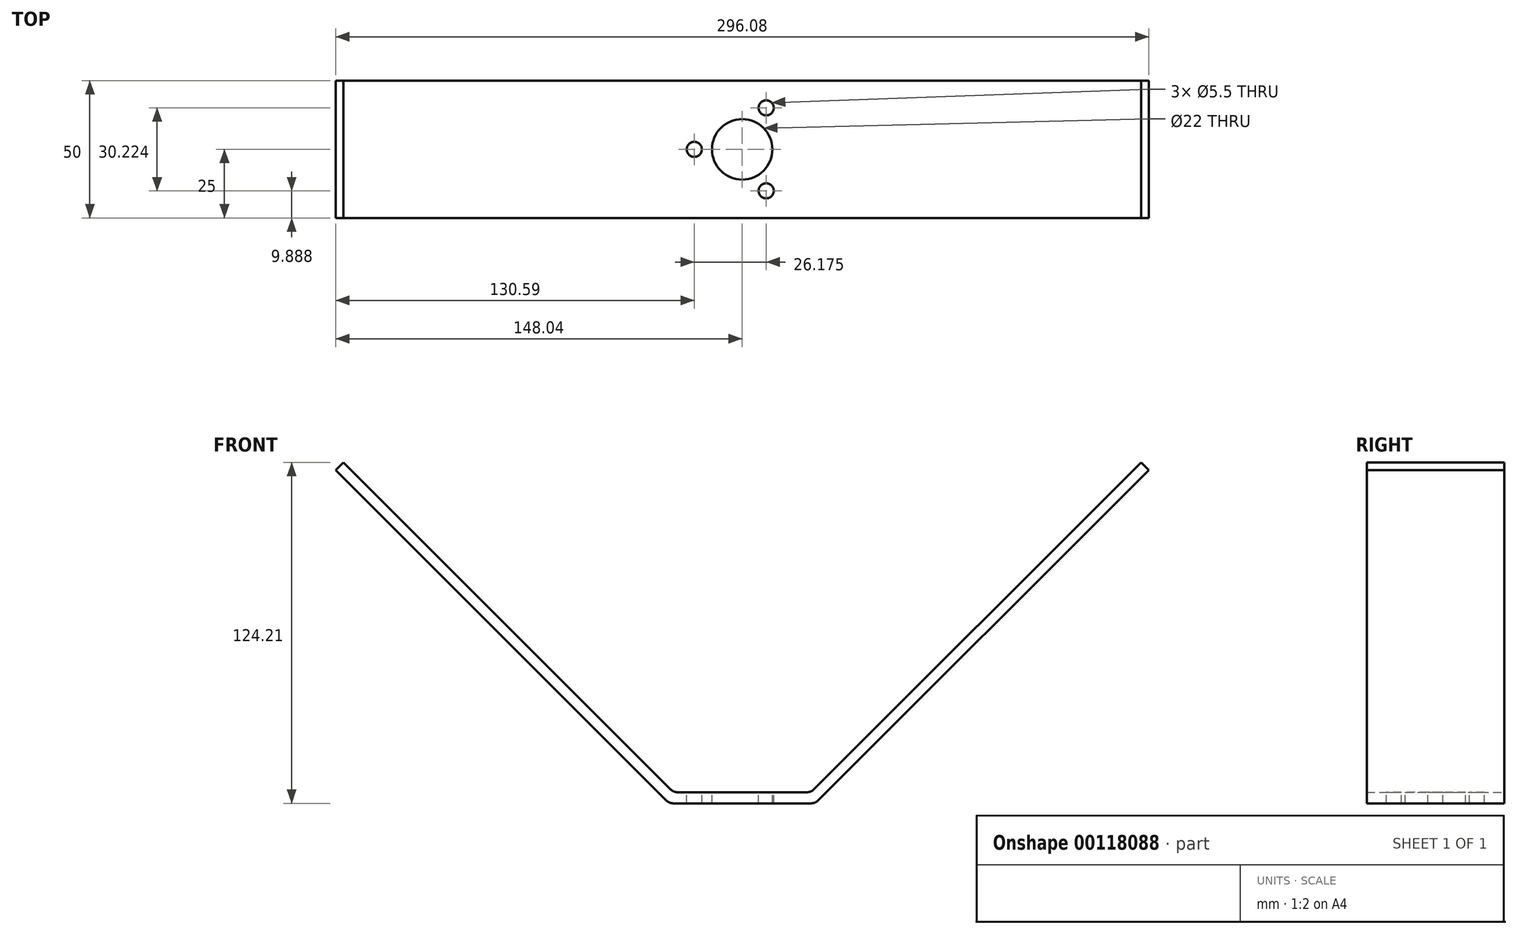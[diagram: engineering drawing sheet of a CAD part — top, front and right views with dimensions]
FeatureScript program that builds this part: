
annotation { "Feature Type Name" : "Feature", "Feature Type Description" : "" }
export const myFeature = defineFeature(function(context is Context, id is Id, definition is map)
    precondition{}
    {
        {
            var Q0;
            Q0=qCreatedBy(makeId("Front.planeOp"),FACE);
            var sketch = newSketch(context, id + "F0", { "sketchPlane" : qUnion([Q0])});
            skLineSegment(sketch, "E0", {"start": v(0, 0) * mm, "end": v(0, -4) * mm});
            skLineSegment(sketch, "E1", {"start": v(0, -4) * mm, "end": v(25, -4) * mm});
            skLineSegment(sketch, "E2", {"start": v(27.83, -2.83) * mm, "end": v(148.04, 117.38) * mm});
            skLineSegment(sketch, "E3", {"start": v(148.04, 117.38) * mm, "end": v(145.2, 120.2) * mm});
            skLineSegment(sketch, "E4", {"start": v(0, 0) * mm, "end": v(23.34, 0) * mm});
            skLineSegment(sketch, "E5", {"start": v(26.17, 1.17) * mm, "end": v(145.2, 120.2) * mm});
            skPoint(sketch, "E6.visualSharp", {"position": v(25, 0) * mm});
            skArc(sketch, "E6.filletArc", {"start": v(23.34, 0) * mm, "mid": v(24.87, 0.3) * mm, "end": v(26.17, 1.17) * mm});
            skPoint(sketch, "E7.visualSharp", {"position": v(26.66, -4) * mm});
            skArc(sketch, "E7.filletArc", {"start": v(25, -4) * mm, "mid": v(26.53, -3.7) * mm, "end": v(27.83, -2.83) * mm});
            skSolve(sketch);
        }
        {
            var Q0;
            Q0=makeQuery(id+"F0.imprint","IMPRINT",FACE,{"disambiguationData":[TD([[makeQuery(id+"F0.imprint","IMPRINT",EDGE,{"derivedFrom":sQuery(id+"F0.wireOp",EDGE,"E0")}),1.0]])]});
            extrude(context, id + "F1", {"entities" : qUnion([Q0]), "endBound" : BoundingType.SYMMETRIC, "depth" : 50 * mm});
        }
        {
            var Q0;
            Q0=makeQuery(id+"F1.opExtrude","SWEPT_BODY",BODY,{"disambiguationData":[OSD([sQuery(id+"F0.wireOp",EDGE,"E0"),sQuery(id+"F0.wireOp",EDGE,"E1"),sQuery(id+"F0.wireOp",EDGE,"E2"),sQuery(id+"F0.wireOp",EDGE,"E3"),sQuery(id+"F0.wireOp",EDGE,"E4"),sQuery(id+"F0.wireOp",EDGE,"E5")])]});
            var Q1;
            Q1=qCreatedBy(makeId("Right.planeOp"),FACE);
            mirror(context, id + "F2", {"operationType" : NewBodyOperationType.ADD, "entities" : qUnion([Q0]), "mirrorPlane" : qUnion([Q1])});
        }
        {
            var Q0;
            {var subQ0=makeQuery(id+"F1.opExtrude","SWEPT_FACE",FACE,{"disambiguationData":[OSD([sQuery(id+"F0.wireOp",EDGE,"E4")])]});Q0=makeQuery(id+"F2.boolean.opBoolean","MERGE",FACE,{"derivedFrom":[subQ0,makeQuery(id+"F2.opPattern","COPY",FACE,{"derivedFrom":subQ0,"instanceName":"1"})]});}
            var sketch = newSketch(context, id + "F3", { "sketchPlane" : qUnion([Q0])});
            skCircle(sketch, "E8", {"center": v(0, 0) * mm, "radius": 11 * mm});
            skCircle(sketch, "E9", {"center": v(0, 0) * mm, "radius": 17.45 * mm, "construction": true});
            skLineSegment(sketch, "E10", {"start": v(0, 0) * mm, "end": v(8.72, -15.11) * mm, "construction": true});
            skLineSegment(sketch, "E11", {"start": v(0, 0) * mm, "end": v(-17.45, 0) * mm, "construction": true});
            skLineSegment(sketch, "E12", {"start": v(0, 0) * mm, "end": v(8.72, 15.11) * mm, "construction": true});
            skSolve(sketch);
        }
        {
            var Q0;
            Q0=sQuery(id+"F3.wireOp",VERTEX,"E11.end");
            var Q1;
            Q1=sQuery(id+"F3.wireOp",VERTEX,"E10.end");
            var Q2;
            Q2=sQuery(id+"F3.wireOp",VERTEX,"E12.end");
            var Q3;
            Q3=makeQuery(id+"F1.opExtrude","SWEPT_BODY",BODY,{"disambiguationData":[OSD([sQuery(id+"F0.wireOp",EDGE,"E0"),sQuery(id+"F0.wireOp",EDGE,"E1"),sQuery(id+"F0.wireOp",EDGE,"E2"),sQuery(id+"F0.wireOp",EDGE,"E3"),sQuery(id+"F0.wireOp",EDGE,"E4"),sQuery(id+"F0.wireOp",EDGE,"E5"),sQuery(id+"F0.wireOp",EDGE,"E6.filletArc"),sQuery(id+"F0.wireOp",EDGE,"E7.filletArc")])]});
            hole(context, id + "F4", {"style" : HoleStyle.SIMPLE, "endStyle" : HoleEndStyle.THROUGH, "standardTappedOrClearance" : lookupTablePath({ "standard" : "ISO", "fit" : "Normal", "size" : "M5", "type" : "Clearance" }), "standardBlindInLast" : lookupTablePath({ "fit" : "Standard", "standard" : "ISO", "size" : "M5", "type" : "Clearance" }), "holeDiameter" : 5.5 * mm, "startFromSketch" : true, "locations" : qUnion([Q0, Q1, Q2]), "scope" : qUnion([Q3]), "isTappedThrough" : true});
        }
        {
            var Q0;
            Q0 = qSketchRegion(id + "F3", true);
            extrude(context, id + "F5", {"entities" : qUnion([Q0]), "operationType" : NewBodyOperationType.REMOVE, "endBound" : BoundingType.UP_TO_NEXT, "oppositeDirection" : true, "depth" : 25 * mm});
        }
    });
